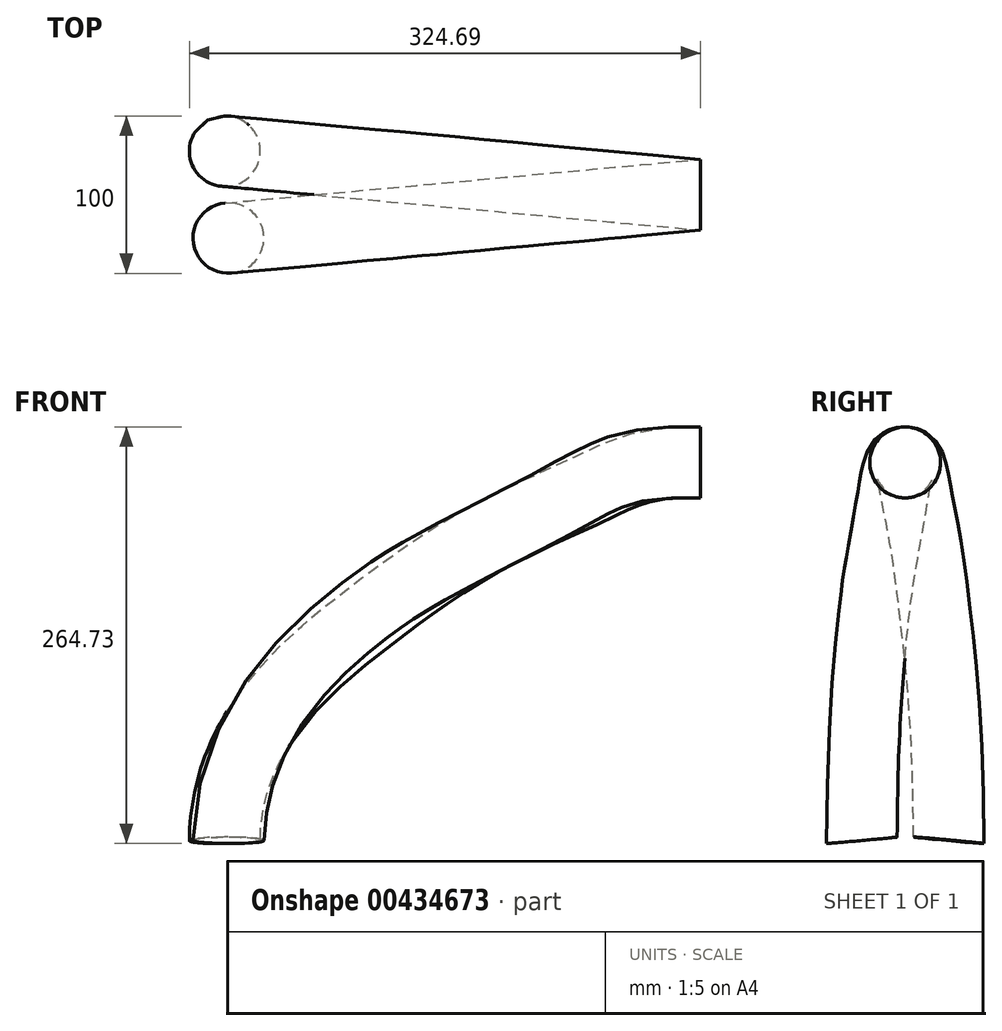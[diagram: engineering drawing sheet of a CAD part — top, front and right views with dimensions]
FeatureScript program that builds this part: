
annotation { "Feature Type Name" : "Feature", "Feature Type Description" : "" }
export const myFeature = defineFeature(function(context is Context, id is Id, definition is map)
    precondition{}
    {
        {
            var Q0;
            Q0=qCreatedBy(makeId("Right.planeOp"),FACE);
            var sketch = newSketch(context, id + "F0", { "sketchPlane" : qUnion([Q0])});
            skLineSegment(sketch, "E0", {"start": v(-21, 300) * mm, "end": v(21, 300) * mm, "construction": true});
            skLineSegment(sketch, "E1", {"start": v(-26, 180) * mm, "end": v(26, 180) * mm, "construction": true});
            skLineSegment(sketch, "E2", {"start": v(-26, 180) * mm, "end": v(-21, 300) * mm, "construction": true});
            skLineSegment(sketch, "E3", {"start": v(21, 300) * mm, "end": v(26, 180) * mm, "construction": true});
            skPoint(sketch, "E4", {"position": v(0, 240) * mm});
            skLineSegment(sketch, "E5", {"start": v(0, 240) * mm, "end": v(-23.5, 240) * mm, "construction": true});
            skCircle(sketch, "E6", {"center": v(0, 240) * mm, "radius": 22.5 * mm});
            skSolve(sketch);
        }
        {
            var Q0;
            Q0=qCreatedBy(makeId("Top.planeOp"),FACE);
            var sketch = newSketch(context, id + "F1", { "sketchPlane" : qUnion([Q0])});
            skLineSegment(sketch, "E7.bottom", {"start": v(-323, 50) * mm, "end": v(-277, 50) * mm, "construction": true});
            skLineSegment(sketch, "E7.top", {"start": v(-323, -50) * mm, "end": v(-277, -50) * mm, "construction": true});
            skLineSegment(sketch, "E7.left", {"start": v(-323, 50) * mm, "end": v(-323, -50) * mm, "construction": true});
            skLineSegment(sketch, "E7.right", {"start": v(-277, 50) * mm, "end": v(-277, -50) * mm, "construction": true});
            skPoint(sketch, "E8", {"position": v(-300, 0) * mm});
            skLineSegment(sketch, "E9", {"start": v(-300, 0) * mm, "end": v(-300, 93.94) * mm, "construction": true});
            skCircle(sketch, "E10", {"center": v(-300, -27.5) * mm, "radius": 22.5 * mm});
            skCircle(sketch, "E11", {"center": v(-300, 27.5) * mm, "radius": 22.5 * mm});
            skLineSegment(sketch, "E12", {"start": v(-300, 93.94) * mm, "end": v(-300, -171.34) * mm, "construction": true});
            skSolve(sketch);
        }
        {
            var Q0;
            Q0=sQuery(id+"F1.wireOp",VERTEX,"E10.center");
            var Q1;
            Q1=sQuery(id+"F0.wireOp",VERTEX,"E4");
            var Q2;
            Q2=qCreatedBy(makeId("Origin.pointOp"),VERTEX);
            cPlane(context, id + "F2", {"entities" : qUnion([Q0, Q1, Q2]), "cplaneType" : CPlaneType.THREE_POINT, "offset" : 25 * mm, "width" : 150 * mm, "height" : 150 * mm});
        }
        {
            var Q0;
            Q0=sQuery(id+"F1.wireOp",VERTEX,"E11.center");
            var Q1;
            Q1=sQuery(id+"F0.wireOp",VERTEX,"E4");
            var Q2;
            Q2=qCreatedBy(makeId("Origin.pointOp"),VERTEX);
            cPlane(context, id + "F3", {"entities" : qUnion([Q0, Q1, Q2]), "cplaneType" : CPlaneType.THREE_POINT, "offset" : 25 * mm, "width" : 150 * mm, "height" : 150 * mm});
        }
        {
            var Q0;
            Q0=qCreatedBy(id+"F2.planeOp",FACE);
            var sketch = newSketch(context, id + "F4", { "sketchPlane" : qUnion([Q0])});
            skFitSpline(sketch, "E13", {"points": [v(-301.62, 0) * mm, v(-216.46, 145) * mm, v(-159.34, 180.8) * mm, v(-80.9, 221.72) * mm, v(0, 240.49) * mm], "startDerivative": vector(17.87, 670.9) * mm, "endDerivative": vector(604.87, -17.73) * mm});
            skSolve(sketch);
        }
        {
            var Q0;
            Q0=qCreatedBy(id+"F3.planeOp",FACE);
            var sketch = newSketch(context, id + "F5", { "sketchPlane" : qUnion([Q0])});
            skFitSpline(sketch, "E14", {"points": [v(-304.1, 0) * mm, v(-209.42, 144.13) * mm, v(-136.18, 192.95) * mm, v(-66.6, 225.91) * mm, v(0, 240.65) * mm], "startDerivative": vector(6.24, 640.44) * mm, "endDerivative": vector(522.05, -15.35) * mm});
            skSolve(sketch);
        }
        {
            var Q0;
            Q0=makeQuery(id+"F0.imprint","IMPRINT",FACE,{"disambiguationData":[TD([[makeQuery(id+"F0.imprint","IMPRINT",EDGE,{"derivedFrom":sQuery(id+"F0.wireOp",EDGE,"E6")}),1.0]])]});
            var Q1;
            Q1=sQuery(id+"F4.wireOp",EDGE,"E13");
            sweep(context, id + "F6", {"profiles" : qUnion([Q0]), "path" : qUnion([Q1])});
        }
        {
            var Q0;
            Q0=makeQuery(id+"F0.imprint","IMPRINT",FACE,{"disambiguationData":[TD([[makeQuery(id+"F0.imprint","IMPRINT",EDGE,{"derivedFrom":sQuery(id+"F0.wireOp",EDGE,"E6")}),1.0]])]});
            var Q1;
            Q1=sQuery(id+"F5.wireOp",EDGE,"E14");
            sweep(context, id + "F7", {"profiles" : qUnion([Q0]), "path" : qUnion([Q1])});
        }
    });
